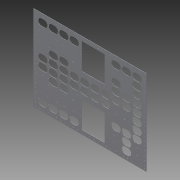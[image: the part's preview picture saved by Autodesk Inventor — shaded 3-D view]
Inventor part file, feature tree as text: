
AUTODESK INVENTOR PART (.ipt)
format: ipt  version: 2014 SP1 (Build 180222100, 222)  size: 851,968 bytes
history: native  units: in
note: dims shown in document units (in); Inventor stores cm internally (conversion verified against a paired STEP export)
features: reference x81, other x6, sketch x5, pattern_linear x2, sheet_metal_op x1, projected_geometry x1
ambient origin geometry x8: Origin, YZ Plane, XZ Plane, XY Plane, X Axis, Y Axis, Z Axis, Center Point
bodies: Solid1 (feature_tree)
feature tree (96):
  sheet_metal_op  "Face1"
  pattern_linear  "Rectangular Pattern2"  Spacing1=7.25in  [1 undecoded]
  pattern_linear  "Rectangular Pattern5"  Spacing1=0.0625in  [1 undecoded]
  sketch  "Sketch1"  dims[d0=27.0in]
  other  "Plate1"
  sketch  "Sketch2"  dims[d1=20.325in]
  sketch  "Sketch4"  dims[d2=0.0625in]
  reference  "Reference4"
  reference  "Reference5"
  sketch  "Sketch12"  dims[d4=7.25in]
  reference  "Reference10"
  reference  "Reference11"
  sketch  "Sketch16"  dims[d5=5.5in d6=7.25in d17=0.0625in d18=0.0in d19=10.6299in d21=1.0in d23=1.0in d24=1.0in d65=0.0625in d66=0.0in d78=11.55in d79=5.5in d80=11.55in d97=0.0625in d98=0.0in d99=7.4803in d101=1.0in d102=0.7874in d104=26.0in d105=0.0625in d106=0.0in d107=1.0in d109=1.8325in d110=2.5in d111=0.125in d112=3.937in d114=1.8325in d115=3.937in d117=2.5in d120=0.0625in d121=0.0in]
  reference  "Reference12"
  reference  "Reference13"
  reference  "Reference14"
  reference  "Reference15"
  reference  "Reference16"
  reference  "Reference17"
  reference  "Reference18"
  reference  "Reference19"
  reference  "Reference20"
  reference  "Reference21"
  reference  "Reference22"
  reference  "Reference23"
  reference  "Reference24"
  reference  "Reference25"
  reference  "Reference26"
  reference  "Reference27"
  reference  "Reference28"
  reference  "Reference29"
  reference  "Reference30"
  reference  "Reference31"
  reference  "Reference32"
  reference  "Reference33"
  reference  "Reference34"
  reference  "Reference35"
  reference  "Reference36"
  reference  "Reference37"
  reference  "Reference38"
  reference  "Reference39"
  reference  "Reference40"
  reference  "Reference41"
  reference  "Reference42"
  reference  "Reference43"
  reference  "Reference44"
  reference  "Reference45"
  reference  "Reference46"
  projected_geometry  "Projected Loop1"
  reference  "Reference47"
  reference  "Reference48"
  reference  "Reference49"
  reference  "Reference50"
  reference  "Reference51"
  reference  "Reference52"
  reference  "Reference53"
  reference  "Reference54"
  reference  "Reference55"
  reference  "Reference56"
  reference  "Reference57"
  reference  "Reference58"
  reference  "Reference59"
  reference  "Reference60"
  reference  "Reference61"
  reference  "Reference62"
  reference  "Reference63"
  reference  "Reference64"
  reference  "Reference65"
  reference  "Reference66"
  reference  "Reference67"
  reference  "Reference68"
  reference  "Reference69"
  reference  "Reference70"
  reference  "Reference71"
  reference  "Reference72"
  reference  "Reference73"
  reference  "Reference74"
  reference  "Reference75"
  reference  "Reference76"
  reference  "Reference77"
  reference  "Reference78"
  reference  "Reference79"
  reference  "Reference80"
  reference  "Reference81"
  reference  "Reference82"
  reference  "Reference83"
  reference  "Reference84"
  reference  "Reference85"
  reference  "Reference86"
  reference  "Reference87"
  reference  "Reference88"
  other  "Cut3"
  other  "Cut6"
  other  "Cut8"
  other  "Cut9"
  other  "Cut10"
note: 2 required parameter values undecoded (feature->parameter linkage not recoverable at this tier; creation-order binding heuristic only, values carry confidence <= 0.55)
